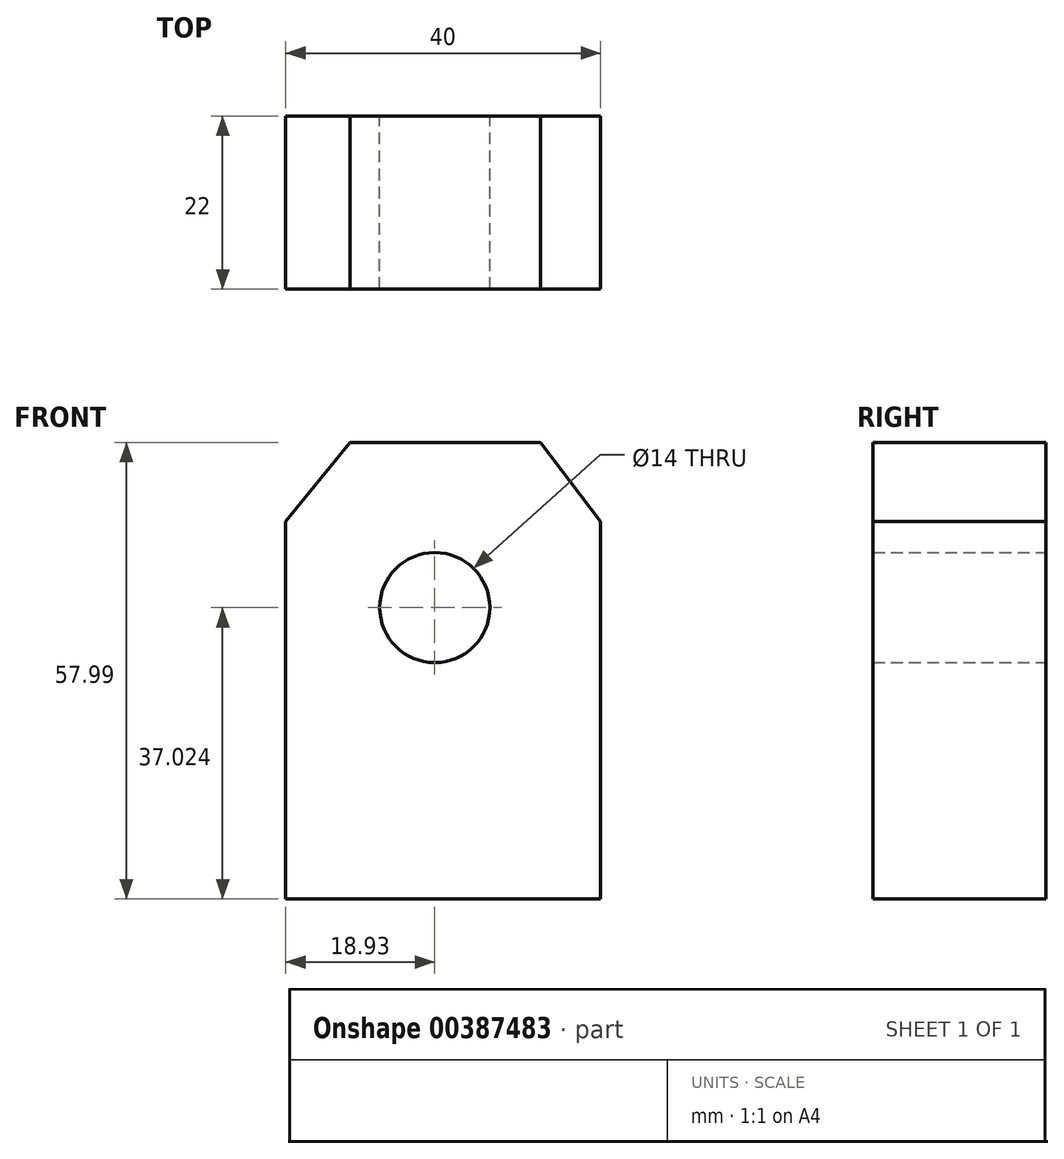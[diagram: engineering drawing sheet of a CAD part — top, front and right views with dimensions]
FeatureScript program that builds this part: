
annotation { "Feature Type Name" : "Feature", "Feature Type Description" : "" }
export const myFeature = defineFeature(function(context is Context, id is Id, definition is map)
    precondition{}
    {
        {
            var Q0;
            Q0=qCreatedBy(makeId("Front.planeOp"),FACE);
            var sketch = newSketch(context, id + "F0", { "sketchPlane" : qUnion([Q0])});
            skLineSegment(sketch, "E0.bottom", {"start": v(-18.93, 0) * mm, "end": v(21.07, 0) * mm});
            skLineSegment(sketch, "E0.left", {"start": v(-18.93, 0) * mm, "end": v(-18.93, 47.98) * mm});
            skLineSegment(sketch, "E0.right", {"start": v(21.07, 0) * mm, "end": v(21.07, 47.98) * mm});
            skPoint(sketch, "E1", {"position": v(13.42, 57.99) * mm});
            skPoint(sketch, "E2", {"position": v(-10.76, 57.99) * mm});
            skLineSegment(sketch, "E3", {"start": v(-18.93, 47.98) * mm, "end": v(-10.76, 57.99) * mm});
            skLineSegment(sketch, "E4", {"start": v(13.42, 57.99) * mm, "end": v(21.07, 47.98) * mm});
            skLineSegment(sketch, "E5", {"start": v(13.42, 57.99) * mm, "end": v(-10.76, 57.99) * mm});
            skSolve(sketch);
        }
        {
            var Q0;
            Q0=makeQuery(id+"F0.imprint","IMPRINT",FACE,{"disambiguationData":[TD([[makeQuery(id+"F0.imprint","IMPRINT",EDGE,{"derivedFrom":sQuery(id+"F0.wireOp",EDGE,"E0.bottom")}),1.0]])]});
            extrude(context, id + "F1", {"entities" : qUnion([Q0]), "depth" : 22 * mm});
        }
        {
            var Q0;
            Q0=qCreatedBy(makeId("Front.planeOp"),FACE);
            var sketch = newSketch(context, id + "F2", { "sketchPlane" : qUnion([Q0])});
            skCircle(sketch, "E6", {"center": v(0, 37.02) * mm, "radius": 7 * mm});
            skSolve(sketch);
        }
        {
            var Q0;
            Q0=makeQuery(id+"F2.imprint","IMPRINT",FACE,{"disambiguationData":[TD([[makeQuery(id+"F2.imprint","IMPRINT",EDGE,{"derivedFrom":sQuery(id+"F2.wireOp",EDGE,"E6")}),1.0]])]});
            var Q1;
            Q1=sQuery(id+"F2.wireOp",EDGE,"E6");
            extrude(context, id + "F3", {"entities" : qUnion([Q0]), "operationType" : NewBodyOperationType.REMOVE, "surfaceEntities" : qUnion([Q1]), "depth" : 57.15 * mm});
        }
    });
